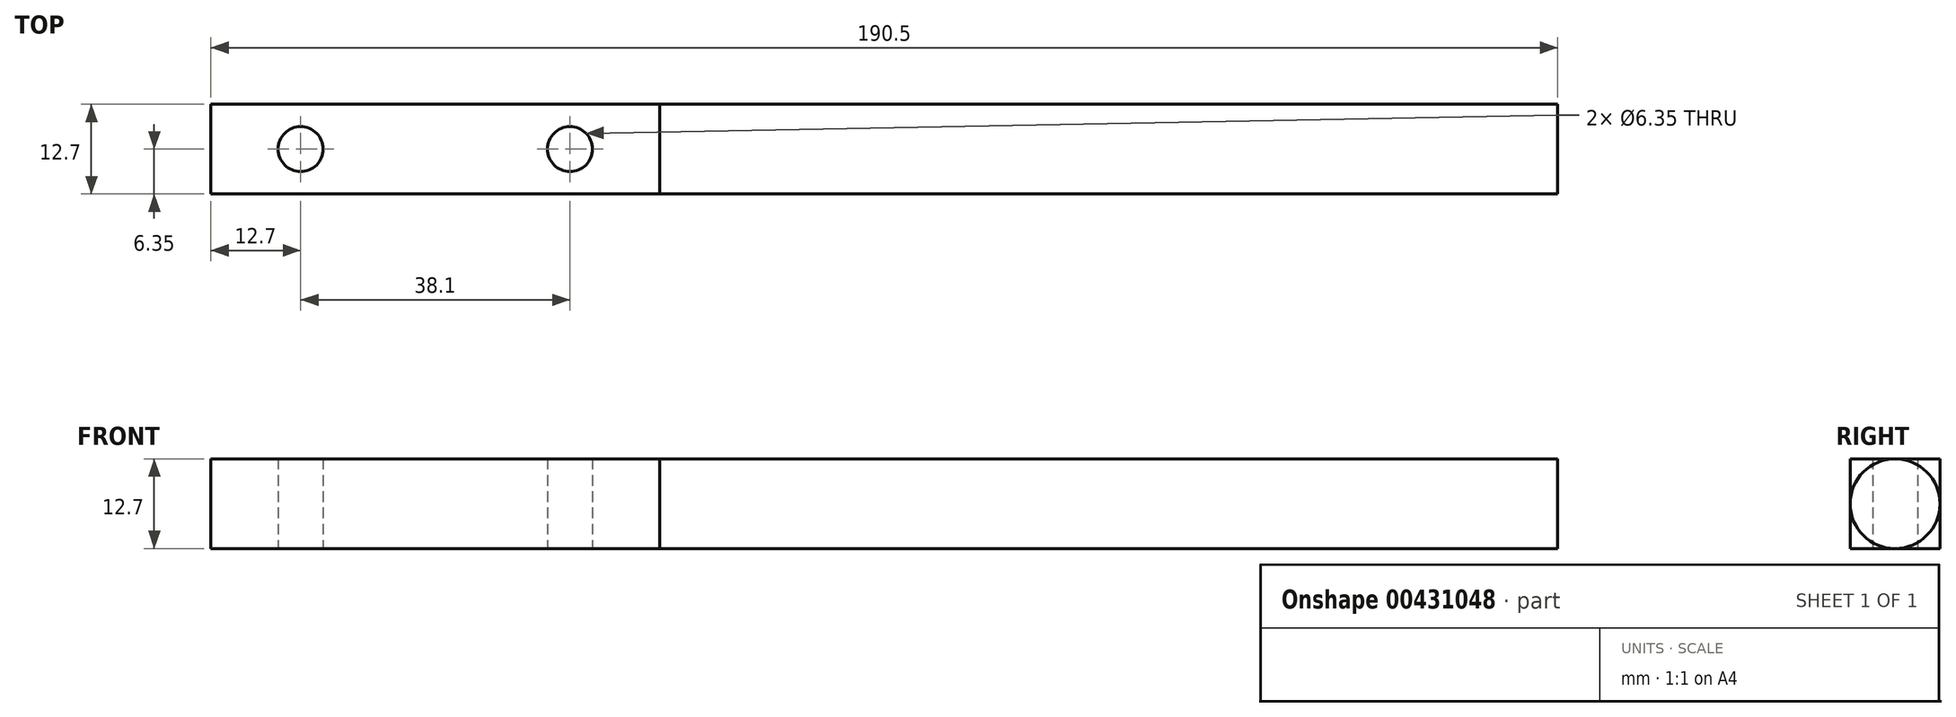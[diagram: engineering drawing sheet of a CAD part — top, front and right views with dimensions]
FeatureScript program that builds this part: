
annotation { "Feature Type Name" : "Feature", "Feature Type Description" : "" }
export const myFeature = defineFeature(function(context is Context, id is Id, definition is map)
    precondition{}
    {
        {
            var Q0;
            Q0=qCreatedBy(makeId("Top.planeOp"),FACE);
            var sketch = newSketch(context, id + "F0", { "sketchPlane" : qUnion([Q0])});
            skLineSegment(sketch, "E0.bottom", {"start": v(-63.5, 6.35) * mm, "end": v(0, 6.35) * mm});
            skLineSegment(sketch, "E0.top", {"start": v(-63.5, -6.35) * mm, "end": v(0, -6.35) * mm});
            skLineSegment(sketch, "E0.left", {"start": v(-63.5, 6.35) * mm, "end": v(-63.5, -6.35) * mm});
            skLineSegment(sketch, "E0.right", {"start": v(0, 6.35) * mm, "end": v(0, -6.35) * mm});
            skPoint(sketch, "E1", {"position": v(0, 0) * mm});
            skCircle(sketch, "E2", {"center": v(-50.8, 0) * mm, "radius": 3.18 * mm});
            skCircle(sketch, "E3", {"center": v(-12.7, 0) * mm, "radius": 3.18 * mm});
            skSolve(sketch);
        }
        {
            var Q0;
            Q0=makeQuery(id+"F0.imprint","IMPRINT",FACE,{"disambiguationData":[TD([[makeQuery(id+"F0.imprint","IMPRINT",EDGE,{"derivedFrom":sQuery(id+"F0.wireOp",EDGE,"E0.bottom")}),-1.0]])]});
            extrude(context, id + "F1", {"entities" : qUnion([Q0]), "endBound" : BoundingType.SYMMETRIC, "depth" : 12.7 * mm});
        }
        {
            var Q0;
            Q0=qCreatedBy(makeId("Top.planeOp"),FACE);
            var sketch = newSketch(context, id + "F2", { "sketchPlane" : qUnion([Q0])});
            skLineSegment(sketch, "E4.bottom", {"start": v(0, 0) * mm, "end": v(127, 0) * mm});
            skLineSegment(sketch, "E4.top", {"start": v(0, 6.35) * mm, "end": v(127, 6.35) * mm});
            skLineSegment(sketch, "E4.left", {"start": v(0, 0) * mm, "end": v(0, 6.35) * mm});
            skLineSegment(sketch, "E4.right", {"start": v(127, 0) * mm, "end": v(127, 6.35) * mm});
            skSolve(sketch);
        }
        {
            var Q0;
            Q0=makeQuery(id+"F2.imprint","IMPRINT",FACE,{"disambiguationData":[TD([[makeQuery(id+"F2.imprint","IMPRINT",EDGE,{"derivedFrom":sQuery(id+"F2.wireOp",EDGE,"E4.bottom")}),1.0]])]});
            var Q1;
            Q1=sQuery(id+"F2.wireOp",EDGE,"E4.bottom");
            revolve(context, id + "F3", {"operationType" : NewBodyOperationType.ADD, "entities" : qUnion([Q0]), "axis" : qUnion([Q1]), "revolveType" : RevolveType.FULL});
        }
    });
